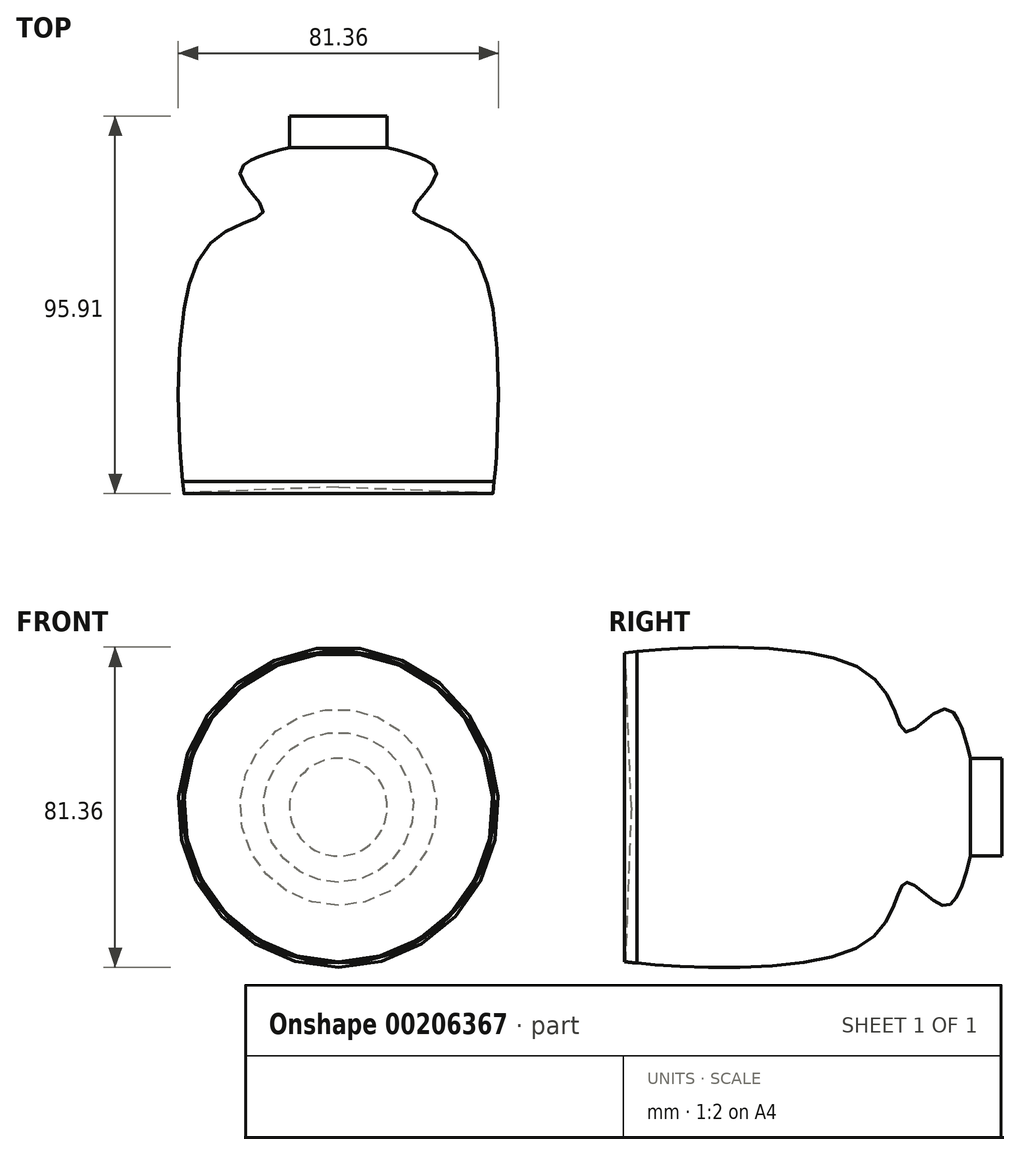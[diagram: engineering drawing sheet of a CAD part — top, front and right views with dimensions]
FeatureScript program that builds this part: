
annotation { "Feature Type Name" : "Feature", "Feature Type Description" : "" }
export const myFeature = defineFeature(function(context is Context, id is Id, definition is map)
    precondition{}
    {
        {
            var Q0;
            Q0=qCreatedBy(makeId("Top.planeOp"),FACE);
            var sketch = newSketch(context, id + "F0", { "sketchPlane" : qUnion([Q0])});
            skLineSegment(sketch, "E0", {"start": v(0, -44.8) * mm, "end": v(0, 49.38) * mm});
            skLineSegment(sketch, "E1", {"start": v(0, 49.38) * mm, "end": v(12.42, 49.38) * mm});
            skLineSegment(sketch, "E2", {"start": v(12.42, 49.38) * mm, "end": v(12.42, 41.38) * mm});
            skFitSpline(sketch, "E3", {"points": [v(12.42, 41.38) * mm, v(24.98, 34.72) * mm, v(19.08, 25.21) * mm, v(34.68, 14.37) * mm, v(39.25, -46.52) * mm, v(39.25, -46.33) * mm], "startDerivative": vector(101.4, -25.96) * mm, "endDerivative": vector(0.68, 14.87) * mm});
            skLineSegment(sketch, "E4", {"start": v(0, -44.8) * mm, "end": v(39.25, -46.33) * mm});
            skLineSegment(sketch, "E5", {"start": v(39.25, -46.52) * mm, "end": v(39.6, -43.4) * mm});
            skSolve(sketch);
        }
        {
            var Q0;
            Q0=makeQuery(id+"F0.imprint","IMPRINT",FACE,{"disambiguationData":[TD([[makeQuery(id+"F0.imprint","IMPRINT",EDGE,{"derivedFrom":sQuery(id+"F0.wireOp",EDGE,"E0")}),-1.0]])]});
            var Q1;
            Q1=sQuery(id+"F0.wireOp",EDGE,"E0");
            revolve(context, id + "F1", {"entities" : qUnion([Q0]), "axis" : qUnion([Q1]), "revolveType" : RevolveType.FULL});
        }
    });
